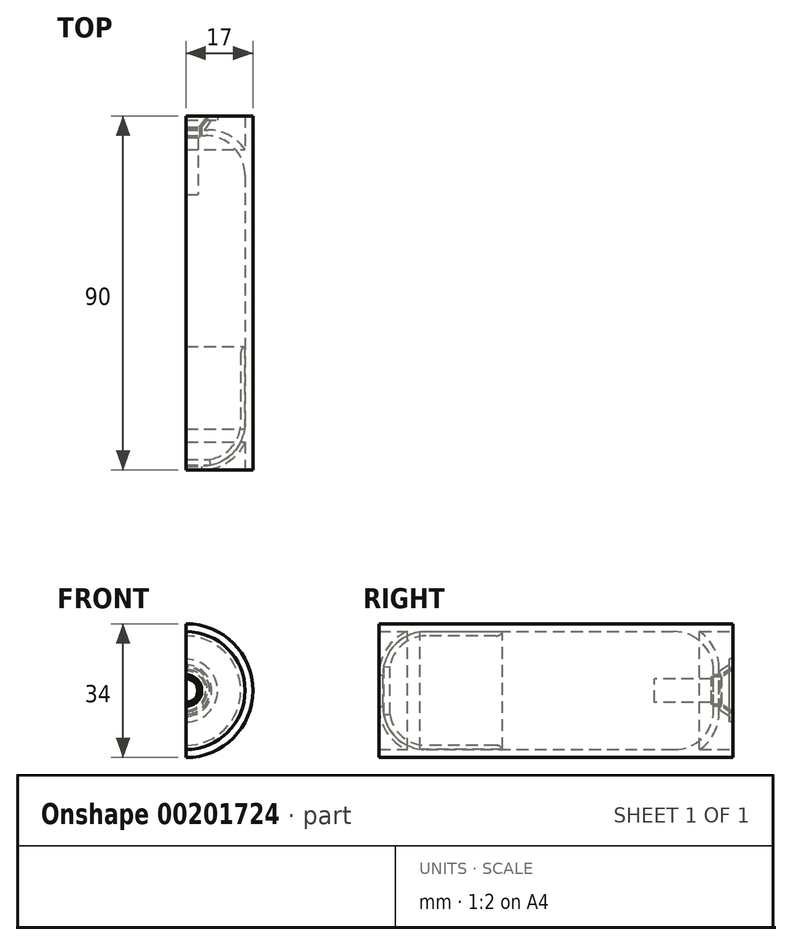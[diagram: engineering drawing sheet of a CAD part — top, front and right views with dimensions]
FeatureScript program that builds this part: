
annotation { "Feature Type Name" : "Feature", "Feature Type Description" : "" }
export const myFeature = defineFeature(function(context is Context, id is Id, definition is map)
    precondition{}
    {
        {
            var Q0;
            Q0=qCreatedBy(makeId("Right.planeOp"),FACE);
            var sketch = newSketch(context, id + "F0", { "sketchPlane" : qUnion([Q0])});
            skLineSegment(sketch, "E0.bottom", {"start": v(-3.13, 34.38) * mm, "end": v(86.87, 34.38) * mm});
            skLineSegment(sketch, "E0.top", {"start": v(-3.13, 32.38) * mm, "end": v(4.08, 32.38) * mm});
            skLineSegment(sketch, "E0.left", {"start": v(-3.13, 34.38) * mm, "end": v(-3.13, 32.38) * mm});
            skLineSegment(sketch, "E0.right", {"start": v(86.87, 34.38) * mm, "end": v(86.87, 32.38) * mm});
            skPoint(sketch, "E0.middle", {"position": v(41.87, 33.38) * mm});
            skLineSegment(sketch, "E1.bottom", {"start": v(86.87, 32.38) * mm, "end": v(81.87, 32.38) * mm, "construction": true});
            skLineSegment(sketch, "E1.top", {"start": v(86.87, 21.38) * mm, "end": v(85.87, 21.38) * mm});
            skLineSegment(sketch, "E1.left", {"start": v(86.87, 32.38) * mm, "end": v(86.87, 21.38) * mm, "construction": true});
            skLineSegment(sketch, "E1.right", {"start": v(81.87, 32.38) * mm, "end": v(81.87, 21.38) * mm, "construction": true});
            skLineSegment(sketch, "E2.bottom", {"start": v(81.87, 32.38) * mm, "end": v(71.87, 32.38) * mm, "construction": true});
            skLineSegment(sketch, "E2.top", {"start": v(81.87, 21.38) * mm, "end": v(71.87, 21.38) * mm, "construction": true});
            skLineSegment(sketch, "E2.right", {"start": v(71.87, 34.38) * mm, "end": v(71.87, 21.38) * mm, "construction": true});
            skLineSegment(sketch, "E3.0", {"start": v(85.87, 22.38) * mm, "end": v(85.37, 22.38) * mm, "construction": true});
            skLineSegment(sketch, "E4.0", {"start": v(85.87, 32.38) * mm, "end": v(85.87, 21.38) * mm, "construction": true});
            skArc(sketch, "E5", {"start": v(83.3, 22.38) * mm, "mid": v(82.12, 28.03) * mm, "end": v(78.34, 32.38) * mm});
            skArc(sketch, "E6", {"start": v(81.87, 21.38) * mm, "mid": v(79.3, 29.1) * mm, "end": v(71.87, 32.38) * mm});
            skLineSegment(sketch, "E7.trimOffspring", {"start": v(78.34, 32.38) * mm, "end": v(86.87, 32.38) * mm});
            skLineSegment(sketch, "E8.top", {"start": v(86.87, 25.38) * mm, "end": v(85.87, 25.38) * mm});
            skLineSegment(sketch, "E8.left", {"start": v(86.87, 23.38) * mm, "end": v(86.87, 25.38) * mm});
            skLineSegment(sketch, "E8.right", {"start": v(85.87, 22.38) * mm, "end": v(85.87, 22.72) * mm, "construction": true});
            skLineSegment(sketch, "E9.bottom", {"start": v(-3.13, 32.38) * mm, "end": v(-2.13, 32.38) * mm, "construction": true});
            skLineSegment(sketch, "E9.top", {"start": v(-3.13, 21.38) * mm, "end": v(-2.13, 21.38) * mm});
            skLineSegment(sketch, "E9.left", {"start": v(-3.13, 32.38) * mm, "end": v(-3.13, 21.38) * mm, "construction": true});
            skLineSegment(sketch, "E9.right", {"start": v(-2.13, 32.38) * mm, "end": v(-2.13, 21.38) * mm, "construction": true});
            skLineSegment(sketch, "E10.bottom", {"start": v(-2.13, 32.38) * mm, "end": v(4.08, 32.38) * mm, "construction": true});
            skLineSegment(sketch, "E10.top", {"start": v(-2.13, 33.38) * mm, "end": v(8.87, 33.38) * mm, "construction": true});
            skLineSegment(sketch, "E10.left", {"start": v(-2.13, 32.38) * mm, "end": v(-2.13, 33.38) * mm, "construction": true});
            skLineSegment(sketch, "E10.right", {"start": v(8.87, 32.38) * mm, "end": v(8.87, 33.38) * mm, "construction": true});
            skArc(sketch, "E11", {"start": v(4.08, 32.38) * mm, "mid": v(-1.17, 27.96) * mm, "end": v(-3.13, 21.38) * mm});
            skArc(sketch, "E12", {"start": v(8.87, 32.38) * mm, "mid": v(1.1, 29.16) * mm, "end": v(-2.13, 21.38) * mm});
            skLineSegment(sketch, "E13.trimOffspring", {"start": v(8.87, 32.38) * mm, "end": v(71.87, 32.38) * mm});
            skLineSegment(sketch, "E14", {"start": v(8.87, 21.38) * mm, "end": v(71.87, 21.38) * mm, "construction": true});
            skLineSegment(sketch, "E15.0", {"start": v(8.87, 17.38) * mm, "end": v(71.87, 17.38) * mm, "construction": true});
            skLineSegment(sketch, "E16.0", {"start": v(86.87, 23.38) * mm, "end": v(85.87, 23.38) * mm, "construction": true});
            skLineSegment(sketch, "E17.0", {"start": v(83.87, 21.38) * mm, "end": v(83.87, 25.38) * mm, "construction": true});
            skLineSegment(sketch, "E18", {"start": v(86.87, 23.38) * mm, "end": v(83.87, 21.38) * mm});
            skLineSegment(sketch, "E19.0", {"start": v(85.87, 23.92) * mm, "end": v(83.57, 22.38) * mm});
            skLineSegment(sketch, "E20.trimOffspring", {"start": v(83.87, 21.38) * mm, "end": v(81.87, 21.38) * mm});
            skLineSegment(sketch, "E21.trimOffspring", {"start": v(83.57, 22.38) * mm, "end": v(83.3, 22.38) * mm});
            skLineSegment(sketch, "E22.trimOffspring", {"start": v(85.87, 23.92) * mm, "end": v(85.87, 25.38) * mm});
            skSolve(sketch);
        }
        {
            var Q0;
            Q0=makeQuery(id+"F0.imprint","IMPRINT",FACE,{"disambiguationData":[TD([[makeQuery(id+"F0.imprint","IMPRINT",EDGE,{"derivedFrom":sQuery(id+"F0.wireOp",EDGE,"E0.bottom")}),-1.0]])]});
            var Q1;
            {var subQ5=sQuery(id+"F0.wireOp",EDGE,"E8.bottom");Q1=makeQuery(id+"F0.imprint","IMPRINT",FACE,{"disambiguationData":[TD([[makeQuery(id+"F0.imprint","IMPRINT",EDGE,{"derivedFrom":subQ5}),-1.0]])]});}
            var Q2;
            {var subQ5=sQuery(id+"F0.wireOp",EDGE,"E8.top");Q2=makeQuery(id+"F0.imprint","IMPRINT",FACE,{"disambiguationData":[TD([[makeQuery(id+"F0.imprint","IMPRINT",EDGE,{"derivedFrom":subQ5}),1.0]])]});}
            var Q3;
            Q3=sQuery(id+"F0.wireOp",EDGE,"E15.0");
            revolve(context, id + "F1", {"entities" : qUnion([Q0, Q1, Q2]), "axis" : qUnion([Q3]), "revolveType" : RevolveType.ONE_DIRECTION, "angle" : 180 * degree});
        }
        {
            var Q0;
            Q0=qCreatedBy(makeId("Right.planeOp"),FACE);
            var sketch = newSketch(context, id + "F2", { "sketchPlane" : qUnion([Q0])});
            skLineSegment(sketch, "E23.bottom", {"start": v(-3.13, 34.38) * mm, "end": v(28.58, 34.38) * mm, "construction": true});
            skLineSegment(sketch, "E23.left", {"start": v(-3.13, 34.38) * mm, "end": v(-3.13, 24.38) * mm, "construction": true});
            skLineSegment(sketch, "E23.right", {"start": v(28.58, 34.38) * mm, "end": v(28.58, 33.28) * mm});
            skLineSegment(sketch, "E24", {"start": v(28.58, 32.58) * mm, "end": v(8.84, 32.58) * mm, "construction": true});
            skArc(sketch, "E25", {"start": v(8.84, 32.58) * mm, "mid": v(1.71, 29.98) * mm, "end": v(-2.07, 23.42) * mm, "construction": true});
            skLineSegment(sketch, "E26.0", {"start": v(28.32, 32.28) * mm, "end": v(7.36, 32.28) * mm});
            skArc(sketch, "E27.0", {"start": v(7.36, 32.28) * mm, "mid": v(1.3, 29.34) * mm, "end": v(-1.88, 23.38) * mm});
            skLineSegment(sketch, "E28.0", {"start": v(26.58, 31.28) * mm, "end": v(8.82, 31.28) * mm});
            skArc(sketch, "E29.0", {"start": v(8.84, 30.88) * mm, "mid": v(2.9, 28.77) * mm, "end": v(-0.35, 23.38) * mm, "construction": true});
            skPoint(sketch, "E30.newPointB", {"position": v(28.58, 24.38) * mm});
            skArc(sketch, "E30.filletArc", {"start": v(26.58, 31.28) * mm, "mid": v(27.58, 31.54) * mm, "end": v(28.32, 32.28) * mm});
            skArc(sketch, "E31", {"start": v(8.82, 31.28) * mm, "mid": v(2.67, 28.95) * mm, "end": v(-0.4, 23.12) * mm});
            skLineSegment(sketch, "E32.trimOffspring", {"start": v(-1.86, 23.48) * mm, "end": v(-0.35, 23.38) * mm});
            skSolve(sketch);
        }
        {
            var Q0;
            Q0 = qSketchRegion(id + "F2", true);
            var Q1;
            Q1=sQuery(id+"F0.wireOp",EDGE,"E15.0");
            revolve(context, id + "F3", {"entities" : qUnion([Q0]), "axis" : qUnion([Q1]), "revolveType" : RevolveType.ONE_DIRECTION, "angle" : 180 * degree});
        }
        {
            var Q0;
            Q0=qCreatedBy(makeId("Right.planeOp"),FACE);
            var sketch = newSketch(context, id + "F4", { "sketchPlane" : qUnion([Q0])});
            skLineSegment(sketch, "E33", {"start": v(86.87, 23.38) * mm, "end": v(83.87, 21.38) * mm, "construction": true});
            skLineSegment(sketch, "E34", {"start": v(83.87, 21.38) * mm, "end": v(81.87, 21.38) * mm, "construction": true});
            skLineSegment(sketch, "E35.0", {"start": v(86.87, 22.78) * mm, "end": v(84.02, 20.88) * mm});
            skLineSegment(sketch, "E36.0", {"start": v(84.02, 20.88) * mm, "end": v(81.37, 20.88) * mm});
            skLineSegment(sketch, "E37", {"start": v(86.87, 22.78) * mm, "end": v(86.87, 17.38) * mm});
            skLineSegment(sketch, "E38.0", {"start": v(66.87, 20.38) * mm, "end": v(66.87, 17.38) * mm});
            skLineSegment(sketch, "E39.0", {"start": v(81.37, 20.88) * mm, "end": v(81.37, 20.38) * mm});
            skLineSegment(sketch, "E40.0", {"start": v(81.37, 20.38) * mm, "end": v(66.87, 20.38) * mm});
            skLineSegment(sketch, "E41", {"start": v(71.87, 17.38) * mm, "end": v(66.87, 17.38) * mm});
            skLineSegment(sketch, "E42", {"start": v(71.87, 17.38) * mm, "end": v(86.87, 17.38) * mm});
            skSolve(sketch);
        }
        {
            var Q0;
            Q0=makeQuery(id+"F4.imprint","IMPRINT",FACE,{"disambiguationData":[TD([[makeQuery(id+"F4.imprint","IMPRINT",EDGE,{"derivedFrom":sQuery(id+"F4.wireOp",EDGE,"E35.0")}),1.0]])]});
            var Q1;
            Q1=sQuery(id+"F0.wireOp",EDGE,"E15.0");
            revolve(context, id + "F5", {"entities" : qUnion([Q0]), "axis" : qUnion([Q1]), "revolveType" : RevolveType.ONE_DIRECTION, "angle" : 180 * degree});
        }
    });
